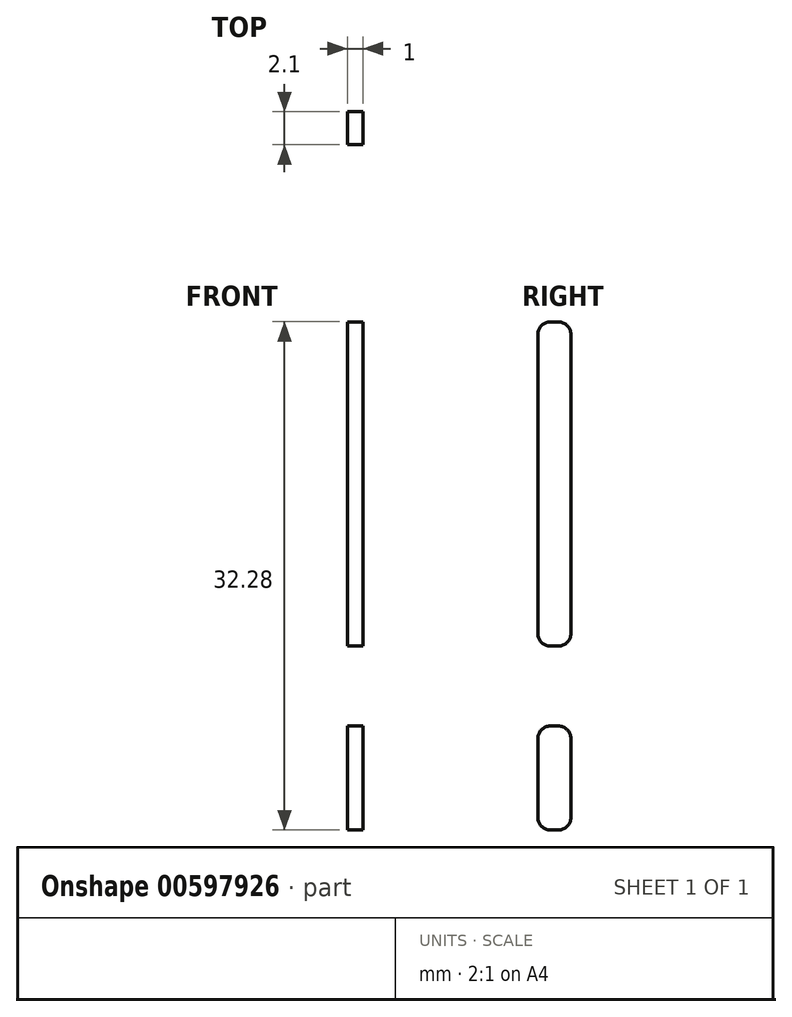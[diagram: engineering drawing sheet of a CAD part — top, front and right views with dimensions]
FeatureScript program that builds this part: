
annotation { "Feature Type Name" : "Feature", "Feature Type Description" : "" }
export const myFeature = defineFeature(function(context is Context, id is Id, definition is map)
    precondition{}
    {
        {
            var Q0;
            Q0=qCreatedBy(makeId("Right.planeOp"),FACE);
            var sketch = newSketch(context, id + "F0", { "sketchPlane" : qUnion([Q0])});
            skLineSegment(sketch, "E0.bottom", {"start": v(-2.23, 120.09) * mm, "end": v(-1.73, 120.09) * mm});
            skLineSegment(sketch, "E0.top", {"start": v(-2.23, 99.49) * mm, "end": v(-1.73, 99.49) * mm});
            skLineSegment(sketch, "E0.left", {"start": v(-3.03, 119.29) * mm, "end": v(-3.03, 100.29) * mm});
            skLineSegment(sketch, "E0.right", {"start": v(-0.93, 119.29) * mm, "end": v(-0.93, 100.29) * mm});
            skPoint(sketch, "E1.oppositeSnap0", {"position": v(-0.93, 109.79) * mm});
            skLineSegment(sketch, "E1.bottom", {"start": v(-2.23, 94.4) * mm, "end": v(-1.73, 94.4) * mm});
            skLineSegment(sketch, "E1.top", {"start": v(-2.23, 87.8) * mm, "end": v(-1.73, 87.8) * mm});
            skLineSegment(sketch, "E1.left", {"start": v(-3.03, 93.6) * mm, "end": v(-3.03, 88.6) * mm});
            skLineSegment(sketch, "E1.right", {"start": v(-0.93, 93.6) * mm, "end": v(-0.93, 88.6) * mm});
            skPoint(sketch, "E2.visualSharp", {"position": v(-3.03, 120.09) * mm});
            skArc(sketch, "E2.filletArc", {"start": v(-2.23, 120.09) * mm, "mid": v(-2.8, 119.85) * mm, "end": v(-3.03, 119.29) * mm});
            skPoint(sketch, "E3.visualSharp", {"position": v(-0.93, 120.09) * mm});
            skArc(sketch, "E3.filletArc", {"start": v(-0.93, 119.29) * mm, "mid": v(-1.16, 119.85) * mm, "end": v(-1.73, 120.09) * mm});
            skPoint(sketch, "E4.visualSharp", {"position": v(-3.03, 99.49) * mm});
            skArc(sketch, "E4.filletArc", {"start": v(-3.03, 100.29) * mm, "mid": v(-2.8, 99.72) * mm, "end": v(-2.23, 99.49) * mm});
            skPoint(sketch, "E5.visualSharp", {"position": v(-0.93, 99.49) * mm});
            skArc(sketch, "E5.filletArc", {"start": v(-1.73, 99.49) * mm, "mid": v(-1.16, 99.72) * mm, "end": v(-0.93, 100.29) * mm});
            skPoint(sketch, "E6.visualSharp", {"position": v(-3.03, 94.4) * mm});
            skArc(sketch, "E6.filletArc", {"start": v(-2.23, 94.4) * mm, "mid": v(-2.8, 94.17) * mm, "end": v(-3.03, 93.6) * mm});
            skPoint(sketch, "E7.visualSharp", {"position": v(-0.93, 87.8) * mm});
            skArc(sketch, "E7.filletArc", {"start": v(-1.73, 87.8) * mm, "mid": v(-1.16, 88.04) * mm, "end": v(-0.93, 88.6) * mm});
            skPoint(sketch, "E8.visualSharp", {"position": v(-3.03, 87.8) * mm});
            skArc(sketch, "E8.filletArc", {"start": v(-3.03, 88.6) * mm, "mid": v(-2.8, 88.04) * mm, "end": v(-2.23, 87.8) * mm});
            skPoint(sketch, "E9.visualSharp", {"position": v(-0.93, 94.4) * mm});
            skArc(sketch, "E9.filletArc", {"start": v(-0.93, 93.6) * mm, "mid": v(-1.16, 94.17) * mm, "end": v(-1.73, 94.4) * mm});
            skSolve(sketch);
        }
        {
            var Q0;
            Q0 = qSketchRegion(id + "F0", true);
            extrude(context, id + "F1", {"entities" : qUnion([Q0]), "depth" : 1 * mm, "offsetDistance" : 25 * mm});
        }
    });
